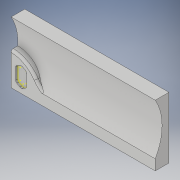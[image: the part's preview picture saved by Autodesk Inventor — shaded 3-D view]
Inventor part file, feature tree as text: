
AUTODESK INVENTOR PART (.ipt)
format: ipt  version: 2018 (Build 220112000, 112)  size: 165,888 bytes
history: native  units: in
note: dims shown in document units (in); Inventor stores cm internally (conversion verified against a paired STEP export)
features: sketch x5, extrude x4, fillet x2, projected_geometry x1
ambient origin geometry x8: Origin, YZ Plane, XZ Plane, XY Plane, X Axis, Y Axis, Z Axis, Center Point
bodies: Solid1 (feature_tree)
feature tree (12):
  extrude  "Extrusion1"  Depth=3.3465in
  extrude  "Extrusion2"  Depth=120.0in TaperAngle=0.0deg
  extrude  "Extrusion6"  Depth=0.125in TaperAngle=0.0deg
  fillet  "Fillet4"  Radius=0.125in
  extrude  "Extrusion7"  Depth=0.6in
  fillet  "Fillet5"  Radius=0.6in
  sketch  "Sketch11"  dims[d30=0.1732in d31=0.13in]
  sketch  "Sketch1"  dims[d0=7.874in d1=3.3465in]
  sketch  "Sketch2"  dims[d2=0.748in d3=0.0in d4=120.0in d5=0.0in]
  sketch  "Sketch9"  dims[d9=0.575in d17=0.5in d18=0.0in d21=0.125in]
  sketch  "Sketch10"  dims[d22=0.1181in d23=0.0in d24=1.108in d29=0.6in]
  projected_geometry  "Projected Loop1"
